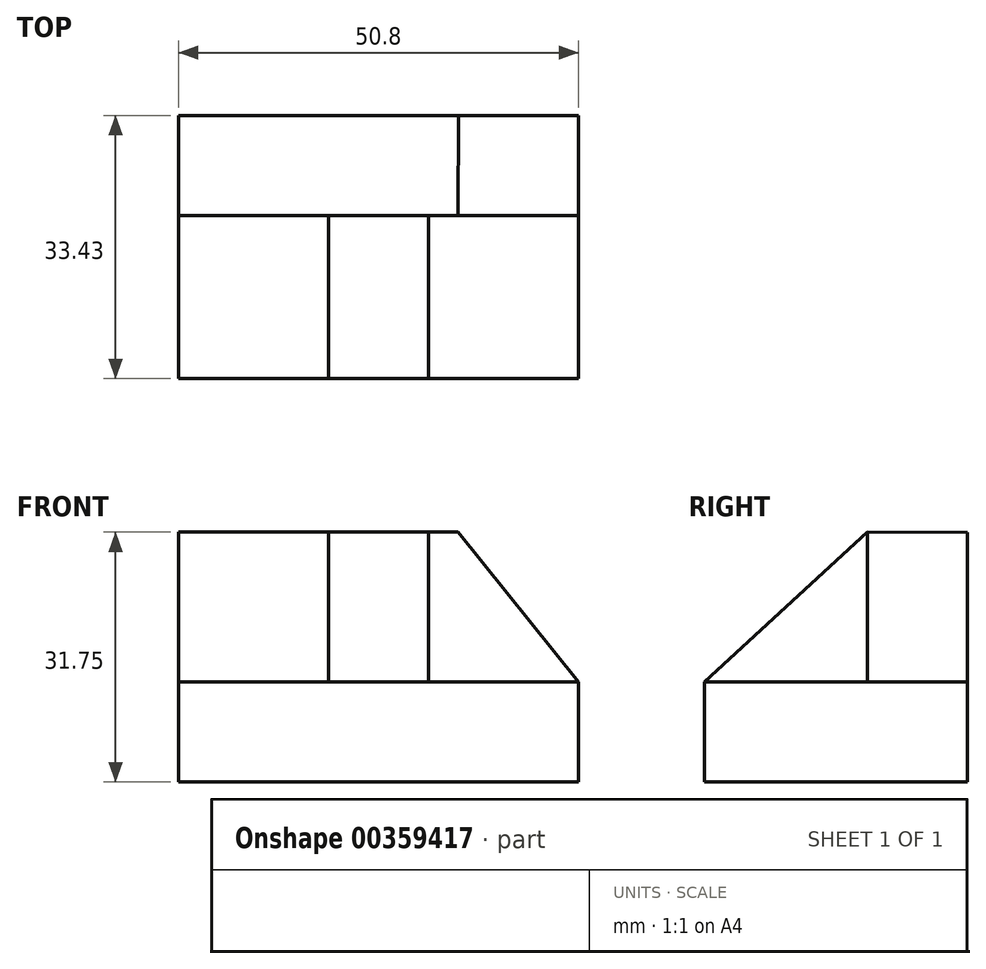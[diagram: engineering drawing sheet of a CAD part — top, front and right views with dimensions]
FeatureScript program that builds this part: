
annotation { "Feature Type Name" : "Feature", "Feature Type Description" : "" }
export const myFeature = defineFeature(function(context is Context, id is Id, definition is map)
    precondition{}
    {
        {
            var Q0;
            Q0=qCreatedBy(makeId("Right.planeOp"),FACE);
            var sketch = newSketch(context, id + "F0", { "sketchPlane" : qUnion([Q0])});
            skLineSegment(sketch, "E0", {"start": v(0, 31.73) * mm, "end": v(0, 0) * mm});
            skLineSegment(sketch, "E1", {"start": v(0, 0) * mm, "end": v(-33.43, 0) * mm});
            skLineSegment(sketch, "E2", {"start": v(-33.43, 0) * mm, "end": v(-33.43, 12.7) * mm});
            skLineSegment(sketch, "E3", {"start": v(-33.43, 12.7) * mm, "end": v(-12.7, 12.7) * mm});
            skLineSegment(sketch, "E4", {"start": v(-12.7, 12.7) * mm, "end": v(-12.7, 31.75) * mm});
            skLineSegment(sketch, "E5", {"start": v(-12.7, 31.75) * mm, "end": v(0, 31.73) * mm});
            skSolve(sketch);
        }
        {
            var Q0;
            Q0=makeQuery(id+"F0.imprint","IMPRINT",FACE,{"disambiguationData":[TD([[makeQuery(id+"F0.imprint","IMPRINT",EDGE,{"derivedFrom":sQuery(id+"F0.wireOp",EDGE,"E0")}),-1.0]])]});
            extrude(context, id + "F1", {"entities" : qUnion([Q0]), "depth" : 50.8 * mm});
        }
        {
            var Q0;
            Q0=makeQuery(id+"F1.opExtrude","SWEPT_FACE",FACE,{"disambiguationData":[OSD([sQuery(id+"F0.wireOp",EDGE,"E4")])]});
            var sketch = newSketch(context, id + "F2", { "sketchPlane" : qUnion([Q0])});
            skLineSegment(sketch, "E6", {"start": v(35.52, 31.75) * mm, "end": v(50.8, 12.7) * mm});
            skLineSegment(sketch, "E7", {"start": v(50.8, 12.7) * mm, "end": v(50.8, 31.75) * mm});
            skLineSegment(sketch, "E8", {"start": v(50.8, 31.75) * mm, "end": v(35.52, 31.75) * mm});
            skSolve(sketch);
        }
        {
            var Q0;
            Q0 = qSketchRegion(id + "F2", true);
            extrude(context, id + "F3", {"entities" : qUnion([Q0]), "operationType" : NewBodyOperationType.REMOVE, "oppositeDirection" : true, "depth" : 25.4 * mm});
        }
        {
            var Q0;
            Q0=makeQuery(id+"F1.opExtrude","SWEPT_FACE",FACE,{"disambiguationData":[OSD([sQuery(id+"F0.wireOp",EDGE,"E3")])]});
            var sketch = newSketch(context, id + "F4", { "sketchPlane" : qUnion([Q0])});
            skLineSegment(sketch, "E9", {"start": v(19.05, -12.7) * mm, "end": v(19.05, -33.43) * mm});
            skLineSegment(sketch, "E10", {"start": v(19.05, -33.43) * mm, "end": v(31.75, -33.43) * mm});
            skLineSegment(sketch, "E11", {"start": v(31.75, -33.43) * mm, "end": v(31.75, -12.7) * mm});
            skLineSegment(sketch, "E12", {"start": v(31.75, -12.7) * mm, "end": v(19.05, -12.7) * mm});
            skSolve(sketch);
        }
        {
            var Q0;
            Q0=makeQuery(id+"F4.imprint","IMPRINT",FACE,{"disambiguationData":[TD([[makeQuery(id+"F4.imprint","IMPRINT",EDGE,{"derivedFrom":sQuery(id+"F4.wireOp",EDGE,"E9")}),1.0]])]});
            extrude(context, id + "F5", {"entities" : qUnion([Q0]), "operationType" : NewBodyOperationType.ADD, "depth" : 19.05 * mm});
        }
        {
            var Q0;
            Q0=makeQuery(id+"F5.opExtrude","SWEPT_FACE",FACE,{"disambiguationData":[OSD([sQuery(id+"F4.wireOp",EDGE,"E11")])]});
            var sketch = newSketch(context, id + "F6", { "sketchPlane" : qUnion([Q0])});
            skLineSegment(sketch, "E13", {"start": v(-33.43, 12.7) * mm, "end": v(-12.7, 31.75) * mm});
            skLineSegment(sketch, "E14", {"start": v(-12.7, 31.75) * mm, "end": v(-33.43, 31.75) * mm});
            skLineSegment(sketch, "E15", {"start": v(-33.43, 31.75) * mm, "end": v(-33.43, 12.7) * mm});
            skSolve(sketch);
        }
        {
            var Q0;
            Q0=makeQuery(id+"F6.imprint","IMPRINT",FACE,{"disambiguationData":[TD([[makeQuery(id+"F6.imprint","IMPRINT",EDGE,{"derivedFrom":sQuery(id+"F6.wireOp",EDGE,"E13")}),1.0]])]});
            extrude(context, id + "F7", {"entities" : qUnion([Q0]), "operationType" : NewBodyOperationType.REMOVE, "oppositeDirection" : true, "depth" : 25.4 * mm});
        }
    });
